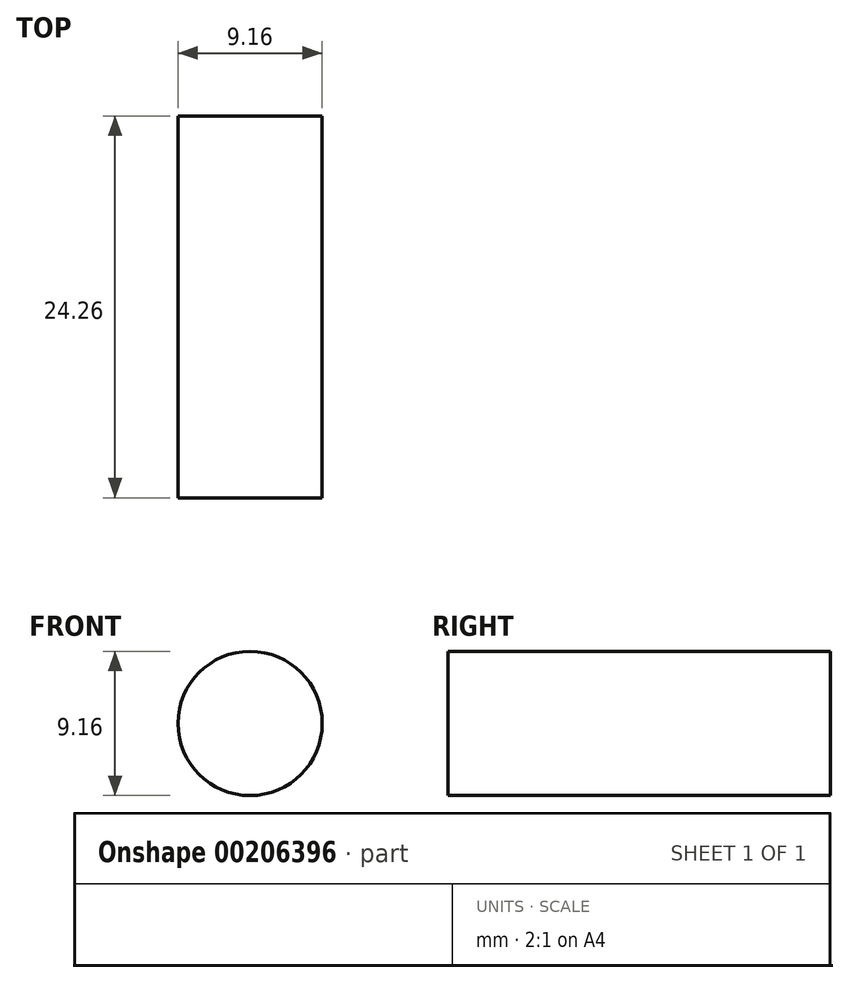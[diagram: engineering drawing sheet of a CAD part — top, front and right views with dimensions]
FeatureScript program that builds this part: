
annotation { "Feature Type Name" : "Feature", "Feature Type Description" : "" }
export const myFeature = defineFeature(function(context is Context, id is Id, definition is map)
    precondition{}
    {
        {
            var Q0;
            Q0=qCreatedBy(makeId("Top.planeOp"),FACE);
            var sketch = newSketch(context, id + "F0", { "sketchPlane" : qUnion([Q0])});
            skLineSegment(sketch, "E0", {"start": v(0, -55.97) * mm, "end": v(-4.58, -55.97) * mm});
            skLineSegment(sketch, "E1", {"start": v(-4.58, -55.97) * mm, "end": v(-4.58, -31.7) * mm});
            skLineSegment(sketch, "E2", {"start": v(-4.58, -31.7) * mm, "end": v(0, -31.7) * mm});
            skLineSegment(sketch, "E3", {"start": v(0, -31.7) * mm, "end": v(0, -55.97) * mm});
            skSolve(sketch);
        }
        {
            var Q0;
            Q0=makeQuery(id+"F0.imprint","IMPRINT",FACE,{"disambiguationData":[TD([[makeQuery(id+"F0.imprint","IMPRINT",EDGE,{"derivedFrom":sQuery(id+"F0.wireOp",EDGE,"E0")}),-1.0]])]});
            var Q1;
            Q1=sQuery(id+"F0.wireOp",EDGE,"E3");
            revolve(context, id + "F1", {"entities" : qUnion([Q0]), "axis" : qUnion([Q1]), "revolveType" : RevolveType.FULL});
        }
        {
            var Q0;
            Q0=qCreatedBy(makeId("Top.planeOp"),FACE);
            var sketch = newSketch(context, id + "F2", { "sketchPlane" : qUnion([Q0])});
            skLineSegment(sketch, "E4", {"start": v(0, 38.57) * mm, "end": v(-5.04, 38.57) * mm});
            skLineSegment(sketch, "E5", {"start": v(-5.04, 38.57) * mm, "end": v(-5.04, -8.13) * mm});
            skLineSegment(sketch, "E6", {"start": v(-5.04, -8.13) * mm, "end": v(0, -8.13) * mm});
            skLineSegment(sketch, "E7", {"start": v(0, -8.13) * mm, "end": v(0, 38.57) * mm});
            skSolve(sketch);
        }
    });
